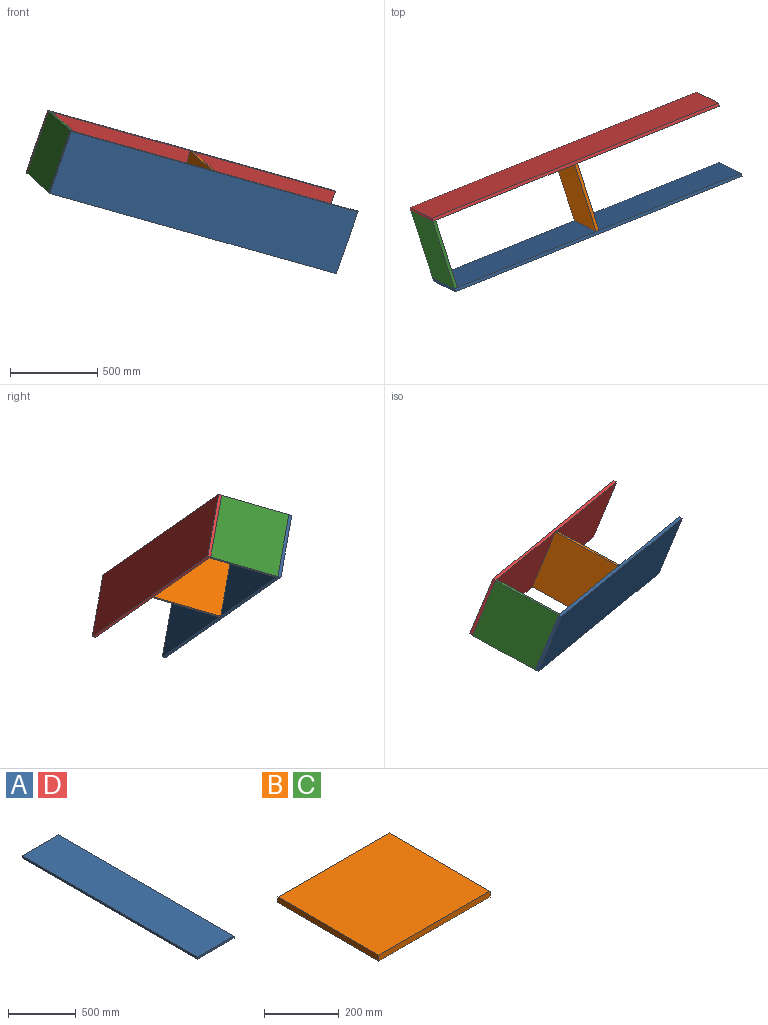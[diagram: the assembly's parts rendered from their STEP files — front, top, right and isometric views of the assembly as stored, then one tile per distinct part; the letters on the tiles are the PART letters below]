
ASSEMBLY  parts=4 mates=3
PART A: 6 faces, bbox 381x1828.8x19.1 mm
  f0: plane 1828.8x381mm, normal (0,0,1), area 696772.8mm2, adj f1,f3,f4,f5
  f1: plane 1828.8x19.05mm, normal (-1,0,0), area 34838.6mm2, adj f0,f2,f4,f5
  f2: plane 1828.8x381mm, normal (0,0,-1), area 696772.8mm2, adj f1,f3,f4,f5
  f3: plane 1828.8x19.05mm, normal (1,0,0), area 34838.6mm2, adj f0,f2,f4,f5
  f4: plane 381x19.05mm, normal (0,-1,0), area 7258mm2, adj f0,f1,f2,f3
  f5: plane 381x19.05mm, normal (0,1,0), area 7258mm2, adj f0,f1,f2,f3
PART B: 6 faces, bbox 419.1x381x19.1 mm
  f0: plane 419.1x381mm, normal (0,0,1), area 159677.1mm2, adj f1,f3,f4,f5
  f1: plane 381x19.05mm, normal (-1,0,0), area 7258.1mm2, adj f0,f2,f4,f5
  f2: plane 419.1x381mm, normal (0,0,-1), area 159677.1mm2, adj f1,f3,f4,f5
  f3: plane 381x19.05mm, normal (1,0,0), area 7258.1mm2, adj f0,f2,f4,f5
  f4: plane 419.1x19.05mm, normal (0,-1,0), area 7983.9mm2, adj f0,f1,f2,f3
  f5: plane 419.1x19.05mm, normal (0,1,0), area 7983.9mm2, adj f0,f1,f2,f3
PART C: same geometry as B
PART D: same geometry as A
PLACE A rot(axis=(0.42,0.78,-0.47),128deg) t=(1203.42,1022.19,-944.22)mm
PLACE B rot(axis=(-0.7,0.63,-0.32),113.3deg) t=(285.69,955.44,-714.69)mm
PLACE C rot(axis=(0.68,-0.33,-0.65),108deg) t=(-417.58,559.28,-127.99)mm
PLACE D rot(axis=(0.42,0.78,-0.47),128deg) t=(1073.96,1424.29,-827.9)mm fixed
MATE planar A.f1 <-> C.f5  axis (0.33,-0.16,0.93) through (-353.87,358.79,-185.7)mm
MATE planar B.f4 <-> D.f1  axis (0.33,-0.16,0.93) through (343.1,1074.25,-304.55)mm
MATE planar C.f5 <-> D.f1  axis (0.33,-0.16,0.93) through (-477.7,743.41,-74.43)mm
